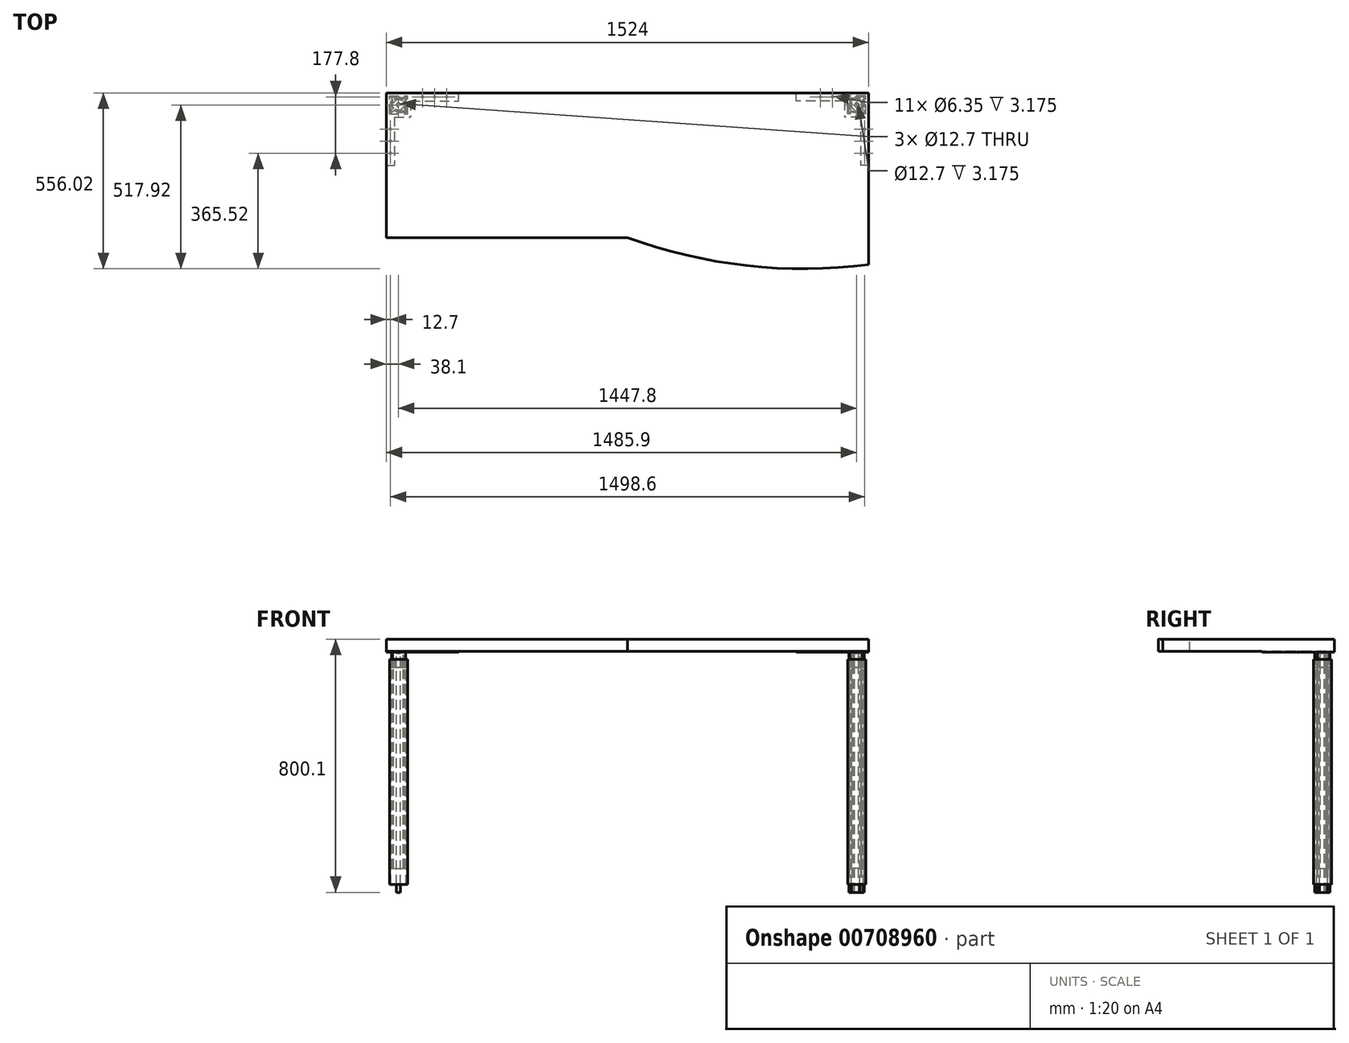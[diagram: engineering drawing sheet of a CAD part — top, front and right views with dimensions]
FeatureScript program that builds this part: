
annotation { "Feature Type Name" : "Feature", "Feature Type Description" : "" }
export const myFeature = defineFeature(function(context is Context, id is Id, definition is map)
    precondition{}
    {
        {
            var Q0;
            Q0=qCreatedBy(makeId("Top.planeOp"),FACE);
            var sketch = newSketch(context, id + "F0", { "sketchPlane" : qUnion([Q0])});
            skLineSegment(sketch, "E0", {"start": v(762, 0) * mm, "end": v(762, 228.6) * mm});
            skLineSegment(sketch, "E1", {"start": v(762, 228.6) * mm, "end": v(0, 228.6) * mm});
            skLineSegment(sketch, "E2.MirrorCS", {"start": v(762, 0) * mm, "end": v(762, -250.9) * mm});
            skLineSegment(sketch, "E3.MirrorCS", {"start": v(-762, 0) * mm, "end": v(-762, 228.6) * mm});
            skLineSegment(sketch, "E4.MirrorCS", {"start": v(-762, 0) * mm, "end": v(-762, -228.6) * mm});
            skLineSegment(sketch, "E5.MirrorCS", {"start": v(-762, -228.6) * mm, "end": v(0, -228.6) * mm});
            skLineSegment(sketch, "E6.MirrorCS", {"start": v(-762, 228.6) * mm, "end": v(0, 228.6) * mm});
            skLineSegment(sketch, "E7", {"start": v(762, -250.9) * mm, "end": v(762, -314.4) * mm});
            skArc(sketch, "E8", {"start": v(0, -228.6) * mm, "mid": v(375.85, -317.25) * mm, "end": v(762, -314.4) * mm});
            skPoint(sketch, "E9.MirrorCS.start.orphan", {"position": v(762, -228.6) * mm});
            skPoint(sketch, "E10.orphan", {"position": v(762, -377.9) * mm});
            skSolve(sketch);
        }
        {
            var Q0;
            Q0=makeQuery(id+"F0.imprint","IMPRINT",FACE,{"disambiguationData":[TD([[makeQuery(id+"F0.imprint","IMPRINT",EDGE,{"derivedFrom":sQuery(id+"F0.wireOp",EDGE,"E0")}),1.0]])]});
            extrude(context, id + "F1", {"entities" : qUnion([Q0]), "oppositeDirection" : true, "depth" : 38.1 * mm, "offsetDistance" : 25.4 * mm});
        }
        {
            var Q0;
            Q0=makeQuery(id+"F1.opExtrude","CAP_FACE",FACE,{"disambiguationData":[OSD([sQuery(id+"F0.wireOp",EDGE,"E0"),sQuery(id+"F0.wireOp",EDGE,"E1"),sQuery(id+"F0.wireOp",EDGE,"E2.MirrorCS"),sQuery(id+"F0.wireOp",EDGE,"E9.MirrorCS"),sQuery(id+"F0.wireOp",EDGE,"E3.MirrorCS"),sQuery(id+"F0.wireOp",EDGE,"E4.MirrorCS"),sQuery(id+"F0.wireOp",EDGE,"E5.MirrorCS"),sQuery(id+"F0.wireOp",EDGE,"E6.MirrorCS")])],"isStart":false});
            var sketch = newSketch(context, id + "F2", { "sketchPlane" : qUnion([Q0])});
            skLineSegment(sketch, "E11.bottom", {"start": v(-762, -228.6) * mm, "end": v(-685.8, -228.6) * mm});
            skLineSegment(sketch, "E11.top", {"start": v(-736.6, -152.4) * mm, "end": v(-685.8, -152.4) * mm});
            skLineSegment(sketch, "E11.left", {"start": v(-762, -228.6) * mm, "end": v(-762, -152.4) * mm});
            skLineSegment(sketch, "E11.right", {"start": v(-685.8, -203.2) * mm, "end": v(-685.8, -152.4) * mm});
            skLineSegment(sketch, "E12", {"start": v(-762, -152.4) * mm, "end": v(-762, 0) * mm});
            skLineSegment(sketch, "E13.0", {"start": v(-736.6, -152.4) * mm, "end": v(-736.6, 0) * mm});
            skLineSegment(sketch, "E14", {"start": v(-685.8, -228.6) * mm, "end": v(-533.4, -228.6) * mm});
            skLineSegment(sketch, "E15.0", {"start": v(-685.8, -203.2) * mm, "end": v(-533.4, -203.2) * mm});
            skLineSegment(sketch, "E16", {"start": v(-533.4, -203.2) * mm, "end": v(-533.4, -228.6) * mm});
            skLineSegment(sketch, "E17", {"start": v(-762, 0) * mm, "end": v(-736.6, 0) * mm});
            skLineSegment(sketch, "E18", {"start": v(0, 0) * mm, "end": v(0, -228.6) * mm});
            skCircle(sketch, "E19", {"center": v(-749.3, -76.2) * mm, "radius": 3.18 * mm});
            skCircle(sketch, "E20", {"center": v(-749.3, -38.1) * mm, "radius": 3.18 * mm});
            skCircle(sketch, "E21", {"center": v(-749.3, -114.3) * mm, "radius": 3.18 * mm});
            skPoint(sketch, "E22.endSnap0", {"position": v(-609.6, -228.6) * mm});
            skCircle(sketch, "E23", {"center": v(-647.7, -215.9) * mm, "radius": 3.18 * mm});
            skCircle(sketch, "E24", {"center": v(-609.6, -215.9) * mm, "radius": 3.18 * mm});
            skCircle(sketch, "E25", {"center": v(-571.5, -215.9) * mm, "radius": 3.18 * mm});
            skLineSegment(sketch, "E26.MirrorCS", {"start": v(762, 0) * mm, "end": v(736.6, 0) * mm});
            skLineSegment(sketch, "E27.MirrorCS", {"start": v(736.6, -152.4) * mm, "end": v(736.6, 0) * mm});
            skCircle(sketch, "E28.MirrorC", {"center": v(749.3, -38.1) * mm, "radius": 3.18 * mm});
            skCircle(sketch, "E29.MirrorC", {"center": v(749.3, -76.2) * mm, "radius": 3.18 * mm});
            skCircle(sketch, "E30.MirrorC", {"center": v(749.3, -114.3) * mm, "radius": 3.18 * mm});
            skLineSegment(sketch, "E31.MirrorCS", {"start": v(762, -152.4) * mm, "end": v(762, 0) * mm});
            skLineSegment(sketch, "E32.MirrorCS", {"start": v(762, -228.6) * mm, "end": v(762, -152.4) * mm});
            skLineSegment(sketch, "E33.MirrorCS", {"start": v(762, -228.6) * mm, "end": v(685.8, -228.6) * mm});
            skLineSegment(sketch, "E34.MirrorCS", {"start": v(685.8, -228.6) * mm, "end": v(533.4, -228.6) * mm});
            skLineSegment(sketch, "E35.MirrorCS", {"start": v(685.8, -203.2) * mm, "end": v(533.4, -203.2) * mm});
            skLineSegment(sketch, "E36.MirrorCS", {"start": v(533.4, -203.2) * mm, "end": v(533.4, -228.6) * mm});
            skCircle(sketch, "E37.MirrorC", {"center": v(609.6, -215.9) * mm, "radius": 3.18 * mm});
            skCircle(sketch, "E38.MirrorC", {"center": v(647.7, -215.9) * mm, "radius": 3.18 * mm});
            skLineSegment(sketch, "E39.MirrorCS", {"start": v(685.8, -203.2) * mm, "end": v(685.8, -152.4) * mm});
            skLineSegment(sketch, "E40.MirrorCS", {"start": v(736.6, -152.4) * mm, "end": v(685.8, -152.4) * mm});
            skLineSegment(sketch, "E41.bottom", {"start": v(-742.95, -171.45) * mm, "end": v(-704.85, -171.45) * mm});
            skLineSegment(sketch, "E41.top", {"start": v(-742.95, -209.55) * mm, "end": v(-704.85, -209.55) * mm});
            skLineSegment(sketch, "E41.right", {"start": v(-704.85, -171.45) * mm, "end": v(-704.85, -209.55) * mm});
            skPoint(sketch, "E41.middle", {"position": v(-723.9, -190.5) * mm});
            skLineSegment(sketch, "E42.0", {"start": v(-701.67, -168.28) * mm, "end": v(-701.67, -212.73) * mm});
            skLineSegment(sketch, "E43.0", {"start": v(-746.12, -168.28) * mm, "end": v(-701.67, -168.28) * mm});
            skLineSegment(sketch, "E44.0", {"start": v(-746.12, -168.28) * mm, "end": v(-746.13, -212.73) * mm});
            skLineSegment(sketch, "E45.0", {"start": v(-746.13, -212.73) * mm, "end": v(-701.67, -212.73) * mm});
            skLineSegment(sketch, "E46.trimOffspring", {"start": v(-742.95, -171.45) * mm, "end": v(-742.95, -209.55) * mm});
            skLineSegment(sketch, "E47.MirrorCS", {"start": v(746.12, -174.63) * mm, "end": v(746.13, -212.73) * mm});
            skLineSegment(sketch, "E48.MirrorCS", {"start": v(742.95, -177.56) * mm, "end": v(742.95, -209.55) * mm});
            skLineSegment(sketch, "E49.MirrorCS", {"start": v(746.12, -212.73) * mm, "end": v(704.85, -212.73) * mm});
            skLineSegment(sketch, "E50.MirrorCS", {"start": v(742.95, -209.55) * mm, "end": v(708.29, -209.55) * mm});
            skLineSegment(sketch, "E51.MirrorCS", {"start": v(742.95, -168.28) * mm, "end": v(701.67, -168.28) * mm});
            skLineSegment(sketch, "E52.MirrorCS", {"start": v(739.5, -171.45) * mm, "end": v(704.85, -171.45) * mm});
            skLineSegment(sketch, "E53.MirrorCS", {"start": v(701.67, -168.28) * mm, "end": v(701.67, -206.38) * mm});
            skLineSegment(sketch, "E54.MirrorCS", {"start": v(704.85, -171.45) * mm, "end": v(704.85, -203.28) * mm});
            skPoint(sketch, "E55.orphan", {"position": v(701.67, -206.2) * mm});
            skPoint(sketch, "E56.orphan", {"position": v(-701.67, -206.2) * mm});
            skLineSegment(sketch, "E57", {"start": v(-745.25, -166.16) * mm, "end": v(-733.44, -177) * mm});
            skLineSegment(sketch, "E58", {"start": v(-748.4, -172.52) * mm, "end": v(-738.1, -182.04) * mm});
            skPoint(sketch, "E59.orphan", {"position": v(-742.95, -174.63) * mm});
            skPoint(sketch, "E60.end.orphan", {"position": v(-742.95, -171.45) * mm});
            skPoint(sketch, "E61.orphan", {"position": v(-704.85, -206.38) * mm});
            skPoint(sketch, "E62.start.orphan", {"position": v(-704.85, -209.55) * mm});
            skLineSegment(sketch, "E63.trimOffspring", {"start": v(-714.33, -203.97) * mm, "end": v(-702.56, -214.84) * mm});
            skLineSegment(sketch, "E64.trimOffspring", {"start": v(-709.65, -198.87) * mm, "end": v(-699.4, -208.29) * mm});
            skLineSegment(sketch, "E65", {"start": v(742.95, -168.28) * mm, "end": v(739.5, -171.45) * mm});
            skLineSegment(sketch, "E66", {"start": v(746.12, -174.62) * mm, "end": v(742.95, -177.56) * mm});
            skPoint(sketch, "E67.MirrorCS.end.orphan", {"position": v(742.95, -174.63) * mm});
            skPoint(sketch, "E67.MirrorCS.start.orphan", {"position": v(746.12, -174.63) * mm});
            skPoint(sketch, "E68.start.orphan", {"position": v(704.85, -209.55) * mm});
            skPoint(sketch, "E69.orphan", {"position": v(704.85, -206.38) * mm});
            skPoint(sketch, "E70.orphan", {"position": v(742.95, -171.45) * mm});
            skLineSegment(sketch, "E71.trimOffspring", {"start": v(704.85, -203.28) * mm, "end": v(701.67, -206.2) * mm});
            skLineSegment(sketch, "E72.trimOffspring", {"start": v(708.29, -209.55) * mm, "end": v(704.85, -212.73) * mm});
            skArc(sketch, "E73", {"start": v(-709.65, -198.87) * mm, "mid": v(-712.72, -178.33) * mm, "end": v(-733.44, -177) * mm});
            skLineSegment(sketch, "E74.bottom", {"start": v(-745.25, -166.16) * mm, "end": v(-699.4, -166.16) * mm});
            skLineSegment(sketch, "E74.top", {"start": v(-748.4, -214.84) * mm, "end": v(-702.56, -214.84) * mm});
            skLineSegment(sketch, "E74.left", {"start": v(-748.4, -172.52) * mm, "end": v(-748.4, -214.84) * mm});
            skLineSegment(sketch, "E74.right", {"start": v(-699.4, -166.16) * mm, "end": v(-699.4, -208.29) * mm});
            skLineSegment(sketch, "E75.bottom", {"start": v(-752.44, -162.03) * mm, "end": v(-695.36, -162.03) * mm});
            skLineSegment(sketch, "E75.top", {"start": v(-752.44, -218.97) * mm, "end": v(-695.36, -218.97) * mm});
            skLineSegment(sketch, "E75.left", {"start": v(-752.44, -162.03) * mm, "end": v(-752.44, -218.97) * mm});
            skLineSegment(sketch, "E75.right", {"start": v(-695.36, -162.03) * mm, "end": v(-695.36, -218.97) * mm});
            skPoint(sketch, "E76.orphan", {"position": v(-699.4, -214.84) * mm});
            skPoint(sketch, "E77.orphan", {"position": v(-748.4, -166.16) * mm});
            skArc(sketch, "E78.trimOffspring", {"start": v(-738.1, -182.04) * mm, "mid": v(-735.1, -202.64) * mm, "end": v(-714.33, -203.97) * mm});
            skCircle(sketch, "E79", {"center": v(-723.9, -190.5) * mm, "radius": 6.35 * mm});
            skLineSegment(sketch, "E80", {"start": v(-748.4, -172.52) * mm, "end": v(-748.4, -166.16) * mm});
            skLineSegment(sketch, "E81", {"start": v(-745.25, -166.16) * mm, "end": v(-748.4, -166.16) * mm});
            skLineSegment(sketch, "E82", {"start": v(-702.56, -214.84) * mm, "end": v(-699.4, -214.84) * mm});
            skLineSegment(sketch, "E83", {"start": v(-699.4, -208.29) * mm, "end": v(-699.4, -214.84) * mm});
            skLineSegment(sketch, "E84.MirrorCS", {"start": v(752.44, -162.03) * mm, "end": v(695.36, -162.03) * mm});
            skLineSegment(sketch, "E85.MirrorCS", {"start": v(752.44, -162.03) * mm, "end": v(752.44, -218.97) * mm});
            skLineSegment(sketch, "E86.MirrorCS", {"start": v(752.44, -218.97) * mm, "end": v(695.36, -218.97) * mm});
            skLineSegment(sketch, "E87.MirrorCS", {"start": v(695.36, -162.03) * mm, "end": v(695.36, -218.97) * mm});
            skLineSegment(sketch, "E88.MirrorCS", {"start": v(745.25, -166.16) * mm, "end": v(699.4, -166.16) * mm});
            skLineSegment(sketch, "E89.MirrorCS", {"start": v(745.25, -166.16) * mm, "end": v(748.4, -166.16) * mm});
            skLineSegment(sketch, "E90.MirrorCS", {"start": v(748.4, -172.52) * mm, "end": v(748.4, -166.16) * mm});
            skLineSegment(sketch, "E91.MirrorCS", {"start": v(748.4, -172.52) * mm, "end": v(748.4, -214.84) * mm});
            skLineSegment(sketch, "E92.MirrorCS", {"start": v(699.4, -166.16) * mm, "end": v(699.4, -208.29) * mm});
            skLineSegment(sketch, "E93.MirrorCS", {"start": v(699.4, -208.29) * mm, "end": v(699.4, -214.84) * mm});
            skLineSegment(sketch, "E94.MirrorCS", {"start": v(702.56, -214.84) * mm, "end": v(699.4, -214.84) * mm});
            skLineSegment(sketch, "E95.MirrorCS", {"start": v(714.33, -203.97) * mm, "end": v(702.56, -214.84) * mm});
            skLineSegment(sketch, "E96.MirrorCS", {"start": v(709.65, -198.87) * mm, "end": v(699.4, -208.29) * mm});
            skArc(sketch, "E97.MirrorCS", {"start": v(709.65, -198.87) * mm, "mid": v(712.72, -178.33) * mm, "end": v(733.44, -177) * mm});
            skArc(sketch, "E98.MirrorCS", {"start": v(738.1, -182.04) * mm, "mid": v(735.1, -202.64) * mm, "end": v(714.33, -203.97) * mm});
            skCircle(sketch, "E99.MirrorC", {"center": v(723.9, -190.5) * mm, "radius": 6.35 * mm});
            skLineSegment(sketch, "E100.MirrorCS", {"start": v(745.25, -166.16) * mm, "end": v(733.44, -177) * mm});
            skLineSegment(sketch, "E101.MirrorCS", {"start": v(748.4, -172.52) * mm, "end": v(738.1, -182.04) * mm});
            skLineSegment(sketch, "E102", {"start": v(748.4, -214.84) * mm, "end": v(702.56, -214.84) * mm});
            skPoint(sketch, "E103.orphan", {"position": v(-746.12, -174.62) * mm});
            skPoint(sketch, "E104.orphan", {"position": v(-742.95, -168.28) * mm});
            skPoint(sketch, "E105.orphan", {"position": v(-701.67, -206.38) * mm});
            skPoint(sketch, "E106.orphan", {"position": v(-704.85, -212.73) * mm});
            skSolve(sketch);
        }
        {
            var Q0;
            Q0=makeQuery(id+"F2.imprint","IMPRINT",FACE,{"disambiguationData":[TD([[makeQuery(id+"F2.imprint","IMPRINT",EDGE,{"derivedFrom":sQuery(id+"F2.wireOp",EDGE,"E11.bottom")}),-1.0]])]});
            var Q1;
            Q1=makeQuery(id+"F2.imprint","IMPRINT",FACE,{"disambiguationData":[TD([[makeQuery(id+"F2.imprint","IMPRINT",EDGE,{"derivedFrom":sQuery(id+"F2.wireOp",EDGE,"E26.MirrorCS")}),1.0]])]});
            var Q2;
            Q2=makeQuery(id+"F2.imprint","IMPRINT",FACE,{"disambiguationData":[TD([[makeQuery(id+"F2.imprint","IMPRINT",EDGE,{"derivedFrom":sQuery(id+"F2.wireOp",EDGE,"E74.bottom")}),1.0]])]});
            var Q3;
            {var subQ3=sQuery(id+"F2.wireOp",EDGE,"E41.top");Q3=makeQuery(id+"F2.imprint","IMPRINT",FACE,{"disambiguationData":[TD([[makeQuery(id+"F2.imprint","IMPRINT",EDGE,{"derivedFrom":subQ3}),-1.0]])]});}
            var Q4;
            {var subQ4=sQuery(id+"F2.wireOp",EDGE,"E44.0");Q4=makeQuery(id+"F2.imprint","IMPRINT",FACE,{"disambiguationData":[TD([[makeQuery(id+"F2.imprint","IMPRINT",EDGE,{"derivedFrom":subQ4}),-1.0]])]});}
            var Q5;
            {var subQ4=sQuery(id+"F2.wireOp",EDGE,"E41.top");Q5=makeQuery(id+"F2.imprint","IMPRINT",FACE,{"disambiguationData":[TD([[makeQuery(id+"F2.imprint","IMPRINT",EDGE,{"derivedFrom":subQ4}),1.0]])]});}
            var Q6;
            {var subQ4=sQuery(id+"F2.wireOp",EDGE,"E41.bottom");Q6=makeQuery(id+"F2.imprint","IMPRINT",FACE,{"disambiguationData":[TD([[makeQuery(id+"F2.imprint","IMPRINT",EDGE,{"derivedFrom":subQ4}),-1.0]])]});}
            var Q7;
            {var subQ5=sQuery(id+"F2.wireOp",EDGE,"E41.bottom");Q7=makeQuery(id+"F2.imprint","IMPRINT",FACE,{"disambiguationData":[TD([[makeQuery(id+"F2.imprint","IMPRINT",EDGE,{"derivedFrom":subQ5}),1.0]])]});}
            var Q8;
            {var subQ5=sQuery(id+"F2.wireOp",EDGE,"E43.0");Q8=makeQuery(id+"F2.imprint","IMPRINT",FACE,{"disambiguationData":[TD([[makeQuery(id+"F2.imprint","IMPRINT",EDGE,{"derivedFrom":subQ5}),1.0]])]});}
            var Q9;
            {var subQ2=sQuery(id+"F2.wireOp",EDGE,"E73");Q9=makeQuery(id+"F2.imprint","IMPRINT",FACE,{"disambiguationData":[TD([[makeQuery(id+"F2.imprint","IMPRINT",EDGE,{"derivedFrom":subQ2}),1.0]])]});}
            var Q10;
            Q10=makeQuery(id+"F2.imprint","IMPRINT",FACE,{"disambiguationData":[TD([[makeQuery(id+"F2.imprint","IMPRINT",EDGE,{"derivedFrom":sQuery(id+"F2.wireOp",EDGE,"E79")}),1.0]])]});
            var Q11;
            {var subQ2=sQuery(id+"F2.wireOp",EDGE,"E47.MirrorCS");Q11=makeQuery(id+"F2.imprint","IMPRINT",FACE,{"disambiguationData":[TD([[makeQuery(id+"F2.imprint","IMPRINT",EDGE,{"derivedFrom":subQ2}),1.0]])]});}
            var Q12;
            {var subQ10=sQuery(id+"F2.wireOp",EDGE,"E89.MirrorCS");Q12=makeQuery(id+"F2.imprint","IMPRINT",FACE,{"disambiguationData":[TD([[makeQuery(id+"F2.imprint","IMPRINT",EDGE,{"derivedFrom":subQ10}),-1.0]])]});}
            var Q13;
            {var subQ4=sQuery(id+"F2.wireOp",EDGE,"E47.MirrorCS");Q13=makeQuery(id+"F2.imprint","IMPRINT",FACE,{"disambiguationData":[TD([[makeQuery(id+"F2.imprint","IMPRINT",EDGE,{"derivedFrom":subQ4}),-1.0]])]});}
            var Q14;
            {var subQ3=sQuery(id+"F2.wireOp",EDGE,"E48.MirrorCS");Q14=makeQuery(id+"F2.imprint","IMPRINT",FACE,{"disambiguationData":[TD([[makeQuery(id+"F2.imprint","IMPRINT",EDGE,{"derivedFrom":subQ3}),-1.0]])]});}
            var Q15;
            {var subQ3=sQuery(id+"F2.wireOp",EDGE,"E52.MirrorCS");Q15=makeQuery(id+"F2.imprint","IMPRINT",FACE,{"disambiguationData":[TD([[makeQuery(id+"F2.imprint","IMPRINT",EDGE,{"derivedFrom":subQ3}),1.0]])]});}
            var Q16;
            {var subQ5=sQuery(id+"F2.wireOp",EDGE,"E51.MirrorCS");Q16=makeQuery(id+"F2.imprint","IMPRINT",FACE,{"disambiguationData":[TD([[makeQuery(id+"F2.imprint","IMPRINT",EDGE,{"derivedFrom":subQ5}),-1.0]])]});}
            var Q17;
            {var subQ2=sQuery(id+"F2.wireOp",EDGE,"E51.MirrorCS");Q17=makeQuery(id+"F2.imprint","IMPRINT",FACE,{"disambiguationData":[TD([[makeQuery(id+"F2.imprint","IMPRINT",EDGE,{"derivedFrom":subQ2}),1.0]])]});}
            var Q18;
            Q18=makeQuery(id+"F2.imprint","IMPRINT",FACE,{"disambiguationData":[TD([[makeQuery(id+"F2.imprint","IMPRINT",EDGE,{"derivedFrom":sQuery(id+"F2.wireOp",EDGE,"E99.MirrorC")}),-1.0]])]});
            var Q19;
            Q19=makeQuery(id+"F2.imprint","IMPRINT",FACE,{"disambiguationData":[TD([[makeQuery(id+"F2.imprint","IMPRINT",EDGE,{"derivedFrom":sQuery(id+"F2.wireOp",EDGE,"E84.MirrorCS")}),1.0]])]});
            extrude(context, id + "F3", {"entities" : qUnion([Q0, Q1, Q2, Q3, Q4, Q5, Q6, Q7, Q8, Q9, Q10, Q11, Q12, Q13, Q14, Q15, Q16, Q17, Q18, Q19]), "depth" : 3.17 * mm, "offsetDistance" : 25.4 * mm});
        }
        {
            var Q0;
            {var subQ0=sQuery(id+"F2.wireOp",EDGE,"E46.trimOffspring");var subQ1=sQuery(id+"F2.wireOp",EDGE,"E41.top");var subQ2=makeQuery(id+"F2.imprint","INTERSECT",VERTEX,{"derivedFrom":[subQ1,subQ0]});Q0=makeQuery(id+"F2.imprint","IMPRINT",FACE,{"disambiguationData":[TD([[makeQuery(id+"F2.imprint","IMPRINT",EDGE,{"disambiguationData":[TD([[subQ2,-1.0]])],"derivedFrom":subQ1}),-1.0]])]});}
            var Q1;
            {var subQ5=sQuery(id+"F2.wireOp",EDGE,"E41.right");var subQ6=sQuery(id+"F2.wireOp",EDGE,"E41.bottom");var subQ7=makeQuery(id+"F2.imprint","INTERSECT",VERTEX,{"derivedFrom":[subQ6,subQ5]});Q1=makeQuery(id+"F2.imprint","IMPRINT",FACE,{"disambiguationData":[TD([[makeQuery(id+"F2.imprint","IMPRINT",EDGE,{"disambiguationData":[TD([[subQ7,1.0]])],"derivedFrom":subQ6}),1.0]])]});}
            var Q2;
            {var subQ4=sQuery(id+"F2.wireOp",EDGE,"E51.MirrorCS");Q2=makeQuery(id+"F2.imprint","IMPRINT",FACE,{"disambiguationData":[TD([[makeQuery(id+"F2.imprint","IMPRINT",EDGE,{"derivedFrom":subQ4}),1.0]])]});}
            var Q3;
            {var subQ3=sQuery(id+"F2.wireOp",EDGE,"E47.MirrorCS");Q3=makeQuery(id+"F2.imprint","IMPRINT",FACE,{"disambiguationData":[TD([[makeQuery(id+"F2.imprint","IMPRINT",EDGE,{"derivedFrom":subQ3}),-1.0]])]});}
            extrude(context, id + "F4", {"entities" : qUnion([Q0, Q1, Q2, Q3]), "operationType" : NewBodyOperationType.ADD, "depth" : 685.8 * mm, "offsetDistance" : 25.4 * mm});
        }
        {
            var Q0;
            {var subQ2=sQuery(id+"F2.wireOp",EDGE,"E73");Q0=makeQuery(id+"F2.imprint","IMPRINT",FACE,{"disambiguationData":[TD([[makeQuery(id+"F2.imprint","IMPRINT",EDGE,{"derivedFrom":subQ2}),1.0]])]});}
            var Q1;
            {var subQ10=sQuery(id+"F2.wireOp",EDGE,"E89.MirrorCS");Q1=makeQuery(id+"F2.imprint","IMPRINT",FACE,{"disambiguationData":[TD([[makeQuery(id+"F2.imprint","IMPRINT",EDGE,{"derivedFrom":subQ10}),-1.0]])]});}
            var Q2;
            {var subQ5=sQuery(id+"F2.wireOp",EDGE,"E41.right");var subQ6=sQuery(id+"F2.wireOp",EDGE,"E41.top");var subQ7=makeQuery(id+"F2.imprint","INTERSECT",VERTEX,{"derivedFrom":[subQ6,subQ5]});Q2=makeQuery(id+"F2.imprint","IMPRINT",FACE,{"disambiguationData":[TD([[makeQuery(id+"F2.imprint","IMPRINT",EDGE,{"disambiguationData":[TD([[subQ7,1.0]])],"derivedFrom":subQ6}),-1.0]])]});}
            var Q3;
            {var subQ4=sQuery(id+"F2.wireOp",EDGE,"E82");Q3=makeQuery(id+"F2.imprint","IMPRINT",FACE,{"disambiguationData":[TD([[makeQuery(id+"F2.imprint","IMPRINT",EDGE,{"derivedFrom":subQ4}),1.0]])]});}
            var Q4;
            {var subQ0=sQuery(id+"F2.wireOp",EDGE,"E46.trimOffspring");var subQ1=sQuery(id+"F2.wireOp",EDGE,"E41.bottom");var subQ2=makeQuery(id+"F2.imprint","INTERSECT",VERTEX,{"derivedFrom":[subQ1,subQ0]});Q4=makeQuery(id+"F2.imprint","IMPRINT",FACE,{"disambiguationData":[TD([[makeQuery(id+"F2.imprint","IMPRINT",EDGE,{"disambiguationData":[TD([[subQ2,-1.0]])],"derivedFrom":subQ1}),1.0]])]});}
            var Q5;
            {var subQ0=sQuery(id+"F2.wireOp",EDGE,"E80");Q5=makeQuery(id+"F2.imprint","IMPRINT",FACE,{"disambiguationData":[TD([[makeQuery(id+"F2.imprint","IMPRINT",EDGE,{"derivedFrom":subQ0}),-1.0]])]});}
            extrude(context, id + "F5", {"entities" : qUnion([Q0, Q1, Q2, Q3, Q4, Q5]), "depth" : 50.8 * mm, "offsetDistance" : 25.4 * mm, "hasSecondDirection" : true, "secondDirectionOppositeDirection" : false, "secondDirectionDepth" : 25.4 * mm});
        }
        {
            var Q0;
            Q0=makeQuery(id+"F2.imprint","IMPRINT",FACE,{"disambiguationData":[TD([[makeQuery(id+"F2.imprint","IMPRINT",EDGE,{"derivedFrom":sQuery(id+"F2.wireOp",EDGE,"E74.bottom")}),1.0]])]});
            var Q1;
            Q1=makeQuery(id+"F2.imprint","IMPRINT",FACE,{"disambiguationData":[TD([[makeQuery(id+"F2.imprint","IMPRINT",EDGE,{"derivedFrom":sQuery(id+"F2.wireOp",EDGE,"E84.MirrorCS")}),1.0]])]});
            extrude(context, id + "F6", {"entities" : qUnion([Q0, Q1]), "operationType" : NewBodyOperationType.ADD, "depth" : 736.6 * mm, "offsetDistance" : 25.4 * mm, "hasSecondDirection" : true, "secondDirectionOppositeDirection" : false, "secondDirectionDepth" : 25.4 * mm});
        }
        {
            var Q0;
            Q0=makeQuery(id+"F2.imprint","IMPRINT",FACE,{"disambiguationData":[TD([[makeQuery(id+"F2.imprint","IMPRINT",EDGE,{"derivedFrom":sQuery(id+"F2.wireOp",EDGE,"E79")}),1.0]])]});
            var Q1;
            Q1=makeQuery(id+"F2.imprint","IMPRINT",FACE,{"disambiguationData":[TD([[makeQuery(id+"F2.imprint","IMPRINT",EDGE,{"derivedFrom":sQuery(id+"F2.wireOp",EDGE,"E99.MirrorC")}),-1.0]])]});
            extrude(context, id + "F7", {"entities" : qUnion([Q0, Q1]), "depth" : 762 * mm, "offsetDistance" : 25.4 * mm, "hasSecondDirection" : true, "secondDirectionOppositeDirection" : false, "secondDirectionDepth" : 6.35 * mm});
        }
    });
